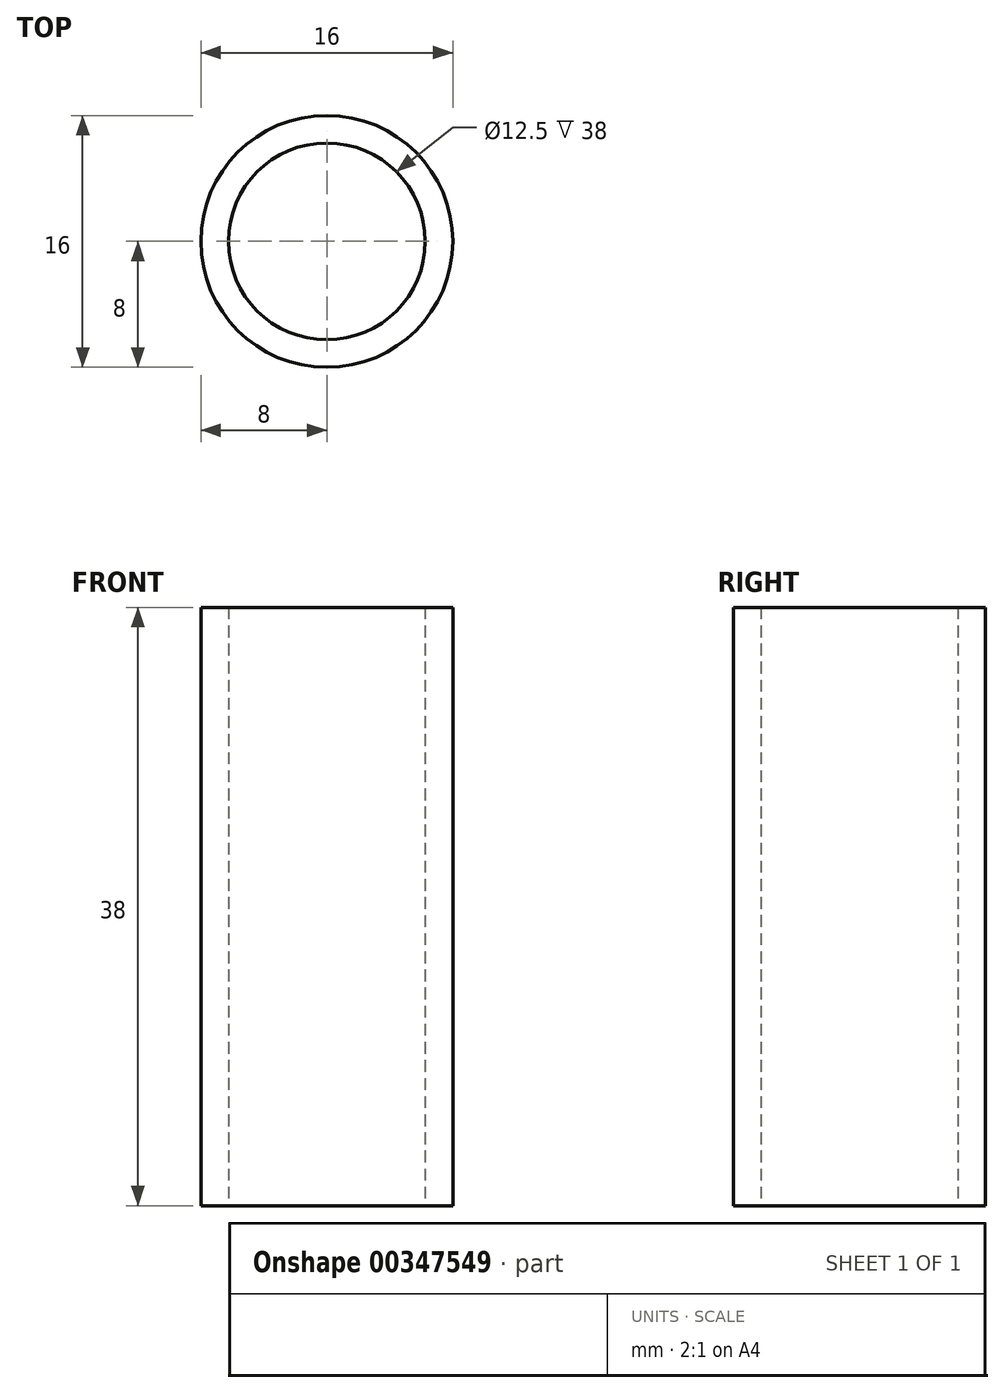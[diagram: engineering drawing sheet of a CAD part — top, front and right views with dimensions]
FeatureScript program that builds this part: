
annotation { "Feature Type Name" : "Feature", "Feature Type Description" : "" }
export const myFeature = defineFeature(function(context is Context, id is Id, definition is map)
    precondition{}
    {
        {
            var Q0;
            Q0=qCreatedBy(makeId("Top.planeOp"),FACE);
            var sketch = newSketch(context, id + "F0", { "sketchPlane" : qUnion([Q0])});
            skCircle(sketch, "E0", {"center": v(0, 0) * mm, "radius": 6.25 * mm});
            skCircle(sketch, "E1", {"center": v(0, 0) * mm, "radius": 8 * mm});
            skSolve(sketch);
        }
        {
            var Q0;
            Q0=makeQuery(id+"F0.imprint","IMPRINT",FACE,{"disambiguationData":[TD([[makeQuery(id+"F0.imprint","IMPRINT",EDGE,{"derivedFrom":sQuery(id+"F0.wireOp",EDGE,"E0")}),-1.0]])]});
            extrude(context, id + "F1", {"entities" : qUnion([Q0]), "endBound" : BoundingType.SYMMETRIC, "depth" : 38 * mm});
        }
    });
